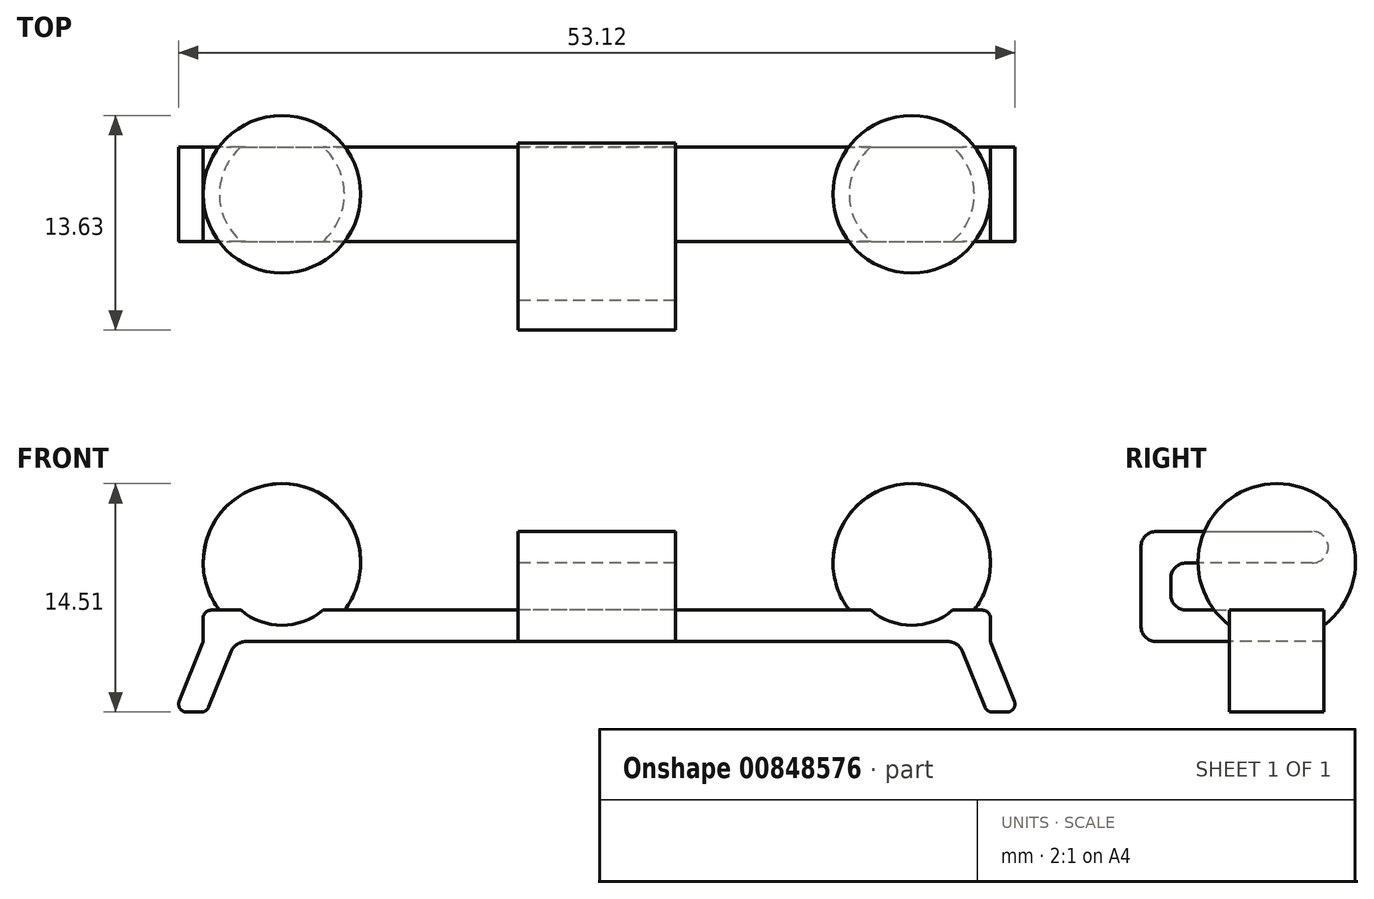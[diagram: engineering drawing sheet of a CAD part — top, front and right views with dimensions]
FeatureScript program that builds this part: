
annotation { "Feature Type Name" : "Feature", "Feature Type Description" : "" }
export const myFeature = defineFeature(function(context is Context, id is Id, definition is map)
    precondition{}
    {
        {
            var Q0;
            Q0=qCreatedBy(makeId("Front.planeOp"),FACE);
            var sketch = newSketch(context, id + "F0", { "sketchPlane" : qUnion([Q0])});
            skLineSegment(sketch, "E0", {"start": v(-22.3, 0) * mm, "end": v(0, 0) * mm});
            skArc(sketch, "E1", {"start": v(-15, 5.08) * mm, "mid": v(-20.04, 10.04) * mm, "end": v(-25, 5) * mm});
            skLineSegment(sketch, "E2", {"start": v(-25, 5) * mm, "end": v(-15, 5.08) * mm});
            skLineSegment(sketch, "E3", {"start": v(0, 0) * mm, "end": v(0, 2) * mm});
            skLineSegment(sketch, "E4", {"start": v(0, 2) * mm, "end": v(-24.5, 2) * mm});
            skLineSegment(sketch, "E5", {"start": v(-25, 1.5) * mm, "end": v(-25, 0.1) * mm});
            skLineSegment(sketch, "E6", {"start": v(-25, 2) * mm, "end": v(-25, 5) * mm, "construction": true});
            skLineSegment(sketch, "E7", {"start": v(-25.04, -0.09) * mm, "end": v(-26.52, -3.79) * mm});
            skLineSegment(sketch, "E8", {"start": v(-26.06, -4.47) * mm, "end": v(-25.11, -4.47) * mm});
            skLineSegment(sketch, "E9", {"start": v(-24.65, -4.16) * mm, "end": v(-23.23, -0.63) * mm});
            skPoint(sketch, "E10.visualSharp", {"position": v(-22.98, 0) * mm});
            skArc(sketch, "E10.filletArc", {"start": v(-22.3, 0) * mm, "mid": v(-22.86, -0.17) * mm, "end": v(-23.23, -0.63) * mm});
            skPoint(sketch, "E11.visualSharp", {"position": v(-26.8, -4.47) * mm});
            skArc(sketch, "E11.filletArc", {"start": v(-26.52, -3.79) * mm, "mid": v(-26.47, -4.25) * mm, "end": v(-26.06, -4.47) * mm});
            skPoint(sketch, "E12.visualSharp", {"position": v(-24.78, -4.47) * mm});
            skArc(sketch, "E12.filletArc", {"start": v(-25.11, -4.47) * mm, "mid": v(-24.84, -4.39) * mm, "end": v(-24.65, -4.16) * mm});
            skPoint(sketch, "E13.visualSharp", {"position": v(-25, 0) * mm});
            skArc(sketch, "E13.filletArc", {"start": v(-25.04, -0.09) * mm, "mid": v(-25, 0) * mm, "end": v(-25, 0.1) * mm});
            skPoint(sketch, "E14.visualSharp", {"position": v(-25, 2) * mm});
            skArc(sketch, "E14.filletArc", {"start": v(-24.5, 2) * mm, "mid": v(-24.85, 1.85) * mm, "end": v(-25, 1.5) * mm});
            skSolve(sketch);
        }
        {
            var Q0;
            Q0=qCreatedBy(makeId("Right.planeOp"),FACE);
            var sketch = newSketch(context, id + "F1", { "sketchPlane" : qUnion([Q0])});
            skLineSegment(sketch, "E15", {"start": v(0, 0) * mm, "end": v(-7.63, 0) * mm});
            skLineSegment(sketch, "E16", {"start": v(-8.63, 1) * mm, "end": v(-8.63, 6) * mm});
            skLineSegment(sketch, "E17", {"start": v(-7.63, 7) * mm, "end": v(2.26, 7) * mm});
            skLineSegment(sketch, "E18", {"start": v(3.26, 6) * mm, "end": v(3.26, 6) * mm});
            skLineSegment(sketch, "E19", {"start": v(2.26, 5) * mm, "end": v(-5.74, 5) * mm});
            skLineSegment(sketch, "E20", {"start": v(-6.74, 4) * mm, "end": v(-6.74, 3) * mm});
            skLineSegment(sketch, "E21", {"start": v(-5.74, 2) * mm, "end": v(0, 2) * mm});
            skLineSegment(sketch, "E22", {"start": v(0, 2) * mm, "end": v(0, 0) * mm});
            skPoint(sketch, "E23.visualSharp", {"position": v(3.26, 5) * mm});
            skArc(sketch, "E23.filletArc", {"start": v(2.26, 5) * mm, "mid": v(2.97, 5.3) * mm, "end": v(3.26, 6) * mm});
            skPoint(sketch, "E24.visualSharp", {"position": v(3.26, 7) * mm});
            skArc(sketch, "E24.filletArc", {"start": v(3.26, 6) * mm, "mid": v(2.97, 6.7) * mm, "end": v(2.26, 7) * mm});
            skPoint(sketch, "E25.visualSharp", {"position": v(-8.63, 7) * mm});
            skArc(sketch, "E25.filletArc", {"start": v(-7.63, 7) * mm, "mid": v(-8.34, 6.7) * mm, "end": v(-8.63, 6) * mm});
            skPoint(sketch, "E26.visualSharp", {"position": v(-6.74, 5) * mm});
            skArc(sketch, "E26.filletArc", {"start": v(-5.74, 5) * mm, "mid": v(-6.45, 4.7) * mm, "end": v(-6.74, 4) * mm});
            skPoint(sketch, "E27.visualSharp", {"position": v(-6.74, 2) * mm});
            skArc(sketch, "E27.filletArc", {"start": v(-6.74, 3) * mm, "mid": v(-6.45, 2.3) * mm, "end": v(-5.74, 2) * mm});
            skPoint(sketch, "E28.visualSharp", {"position": v(-8.63, 0) * mm});
            skArc(sketch, "E28.filletArc", {"start": v(-8.63, 1) * mm, "mid": v(-8.34, 0.3) * mm, "end": v(-7.63, 0) * mm});
            skSolve(sketch);
        }
        {
            var Q0;
            Q0=makeQuery(id+"F0.imprint","IMPRINT",FACE,{"disambiguationData":[TD([[makeQuery(id+"F0.imprint","IMPRINT",EDGE,{"derivedFrom":sQuery(id+"F0.wireOp",EDGE,"E1")}),1.0]])]});
            var Q1;
            Q1=sQuery(id+"F0.wireOp",EDGE,"E2");
            revolve(context, id + "F2", {"surfaceOperationType" : NewSurfaceOperationType.NEW, "entities" : qUnion([Q0]), "axis" : qUnion([Q1]), "revolveType" : RevolveType.FULL});
        }
        {
            var Q0;
            {var subQ0=sQuery(id+"F0.wireOp",EDGE,"E7");Q0=makeQuery(id+"F0.imprint","IMPRINT",FACE,{"disambiguationData":[TD([[makeQuery(id+"F0.imprint","IMPRINT",EDGE,{"derivedFrom":subQ0}),1.0]])]});}
            var Q1;
            {var subQ0=sQuery(id+"F0.wireOp",EDGE,"E3");Q1=makeQuery(id+"F0.imprint","IMPRINT",FACE,{"disambiguationData":[TD([[makeQuery(id+"F0.imprint","IMPRINT",EDGE,{"derivedFrom":subQ0}),1.0]])]});}
            extrude(context, id + "F3", {"entities" : qUnion([Q0, Q1]), "oppositeDirection" : true, "depth" : 3 * mm, "offsetDistance" : 25.4 * mm, "hasSecondDirection" : true, "secondDirectionOppositeDirection" : false, "secondDirectionDepth" : 3 * mm});
        }
        {
            var Q0;
            Q0=makeQuery(id+"F2.opRevolve","SWEPT_BODY",BODY,{"disambiguationData":[OSD([sQuery(id+"F0.wireOp",EDGE,"E1"),sQuery(id+"F0.wireOp",EDGE,"E2")])]});
            var Q1;
            Q1=makeQuery(id+"F3.opExtrude","SWEPT_BODY",BODY,{"disambiguationData":[OSD([sQuery(id+"F0.wireOp",EDGE,"E0"),sQuery(id+"F0.wireOp",EDGE,"E3"),sQuery(id+"F0.wireOp",EDGE,"E4"),sQuery(id+"F0.wireOp",EDGE,"E5"),sQuery(id+"F0.wireOp",EDGE,"E7"),sQuery(id+"F0.wireOp",EDGE,"E8"),sQuery(id+"F0.wireOp",EDGE,"E9")])]});
            var Q2;
            Q2=qCreatedBy(makeId("Right.planeOp"),FACE);
            mirror(context, id + "F4", {"operationType" : NewBodyOperationType.ADD, "entities" : qUnion([Q0, Q1]), "mirrorPlane" : qUnion([Q2])});
        }
        {
            var Q0;
            Q0=makeQuery(id+"F1.imprint","IMPRINT",FACE,{"disambiguationData":[TD([[makeQuery(id+"F1.imprint","IMPRINT",EDGE,{"derivedFrom":sQuery(id+"F1.wireOp",EDGE,"E15")}),-1.0]])]});
            extrude(context, id + "F5", {"entities" : qUnion([Q0]), "operationType" : NewBodyOperationType.ADD, "depth" : 5 * mm, "offsetDistance" : 25 * mm, "hasSecondDirection" : true, "secondDirectionOppositeDirection" : true, "secondDirectionDepth" : 5 * mm});
        }
    });
